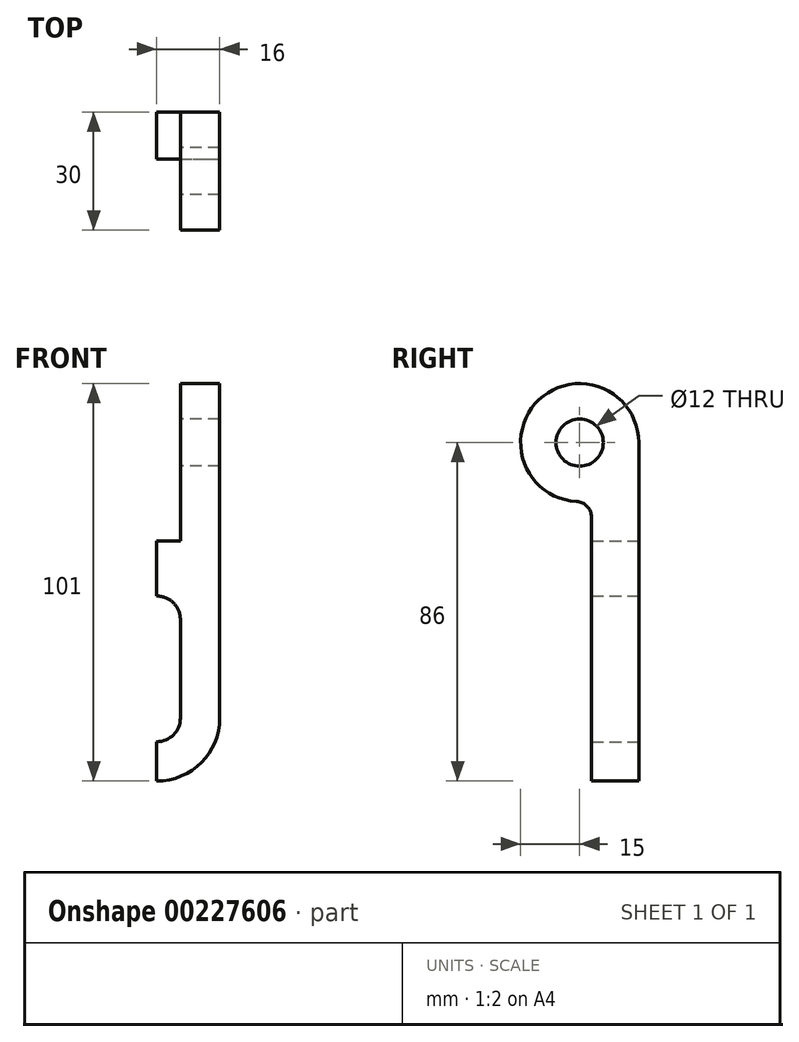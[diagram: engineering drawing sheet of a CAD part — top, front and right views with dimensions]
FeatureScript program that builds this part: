
annotation { "Feature Type Name" : "Feature", "Feature Type Description" : "" }
export const myFeature = defineFeature(function(context is Context, id is Id, definition is map)
    precondition{}
    {
        {
            var Q0;
            Q0=qCreatedBy(makeId("Front.planeOp"),FACE);
            var sketch = newSketch(context, id + "F0", { "sketchPlane" : qUnion([Q0])});
            skLineSegment(sketch, "E0", {"start": v(0, 0) * mm, "end": v(0, 0) * mm});
            skPoint(sketch, "E0.endSnap0", {"position": v(0, 0) * mm});
            skArc(sketch, "E1", {"start": v(-6, 0) * mm, "mid": v(0, -6) * mm, "end": v(6, 0) * mm});
            skArc(sketch, "E2", {"start": v(6, 25) * mm, "mid": v(0, 31) * mm, "end": v(-6, 25) * mm});
            skArc(sketch, "E3", {"start": v(-16, 0) * mm, "mid": v(0, -16) * mm, "end": v(16, 0) * mm});
            skLineSegment(sketch, "E4", {"start": v(-6, 25) * mm, "end": v(-6, 0) * mm});
            skLineSegment(sketch, "E5", {"start": v(6, 25) * mm, "end": v(6, 0) * mm});
            skLineSegment(sketch, "E6", {"start": v(-16, 85) * mm, "end": v(-6, 85) * mm});
            skLineSegment(sketch, "E7", {"start": v(-6, 85) * mm, "end": v(-6, 45) * mm});
            skLineSegment(sketch, "E8", {"start": v(-6, 45) * mm, "end": v(6, 45) * mm});
            skLineSegment(sketch, "E9", {"start": v(6, 45) * mm, "end": v(6, 85) * mm});
            skLineSegment(sketch, "E10", {"start": v(6, 85) * mm, "end": v(16, 85) * mm});
            skLineSegment(sketch, "E11", {"start": v(16, 0) * mm, "end": v(16, 85) * mm});
            skLineSegment(sketch, "E12", {"start": v(-16, 85) * mm, "end": v(-16, 0) * mm});
            skSolve(sketch);
        }
        {
            var Q0;
            Q0=makeQuery(id+"F0.imprint","IMPRINT",FACE,{"disambiguationData":[TD([[makeQuery(id+"F0.imprint","IMPRINT",EDGE,{"derivedFrom":sQuery(id+"F0.wireOp",EDGE,"E1")}),-1.0]])]});
            extrude(context, id + "F1", {"entities" : qUnion([Q0]), "depth" : 30 * mm});
        }
        {
            var Q0;
            Q0=qCreatedBy(makeId("Right.planeOp"),FACE);
            var sketch = newSketch(context, id + "F2", { "sketchPlane" : qUnion([Q0])});
            skLineSegment(sketch, "E13.0", {"start": v(-30, 0) * mm, "end": v(-30, 85) * mm, "construction": true});
            skLineSegment(sketch, "E14.0.0", {"start": v(0, 0) * mm, "end": v(0, 85) * mm, "construction": true});
            skLineSegment(sketch, "E14.0.1", {"start": v(0, 85) * mm, "end": v(-30, 85) * mm, "construction": true});
            skLineSegment(sketch, "E14.0.2", {"start": v(-30, 85) * mm, "end": v(-30, 0) * mm, "construction": true});
            skLineSegment(sketch, "E14.0.3", {"start": v(-30, 0) * mm, "end": v(0, 0) * mm, "construction": true});
            skLineSegment(sketch, "E15", {"start": v(0, -16) * mm, "end": v(-30, -16) * mm, "construction": true});
            skCircle(sketch, "E16", {"center": v(-15, 70) * mm, "radius": 6 * mm});
            skArc(sketch, "E17", {"start": v(0, 70) * mm, "mid": v(-25.32, 80.88) * mm, "end": v(-15.79, 55.02) * mm});
            skLineSegment(sketch, "E18", {"start": v(-12, 51.03) * mm, "end": v(-12, -16) * mm});
            skPoint(sketch, "E18.endSnap0", {"position": v(-15, -16) * mm});
            skLineSegment(sketch, "E19", {"start": v(-12, -16) * mm, "end": v(-30, -16) * mm});
            skLineSegment(sketch, "E20", {"start": v(-30, -16) * mm, "end": v(-30, 70) * mm});
            skPoint(sketch, "E21.visualSharp", {"position": v(-12, 55.3) * mm});
            skArc(sketch, "E21.filletArc", {"start": v(-12, 51.03) * mm, "mid": v(-13.1, 53.78) * mm, "end": v(-15.79, 55.02) * mm});
            skLineSegment(sketch, "E22", {"start": v(-12, -16) * mm, "end": v(0, -16) * mm});
            skLineSegment(sketch, "E23", {"start": v(0, 85) * mm, "end": v(-30, 85) * mm});
            skLineSegment(sketch, "E24", {"start": v(-30, 85) * mm, "end": v(-30, 70) * mm});
            skLineSegment(sketch, "E25", {"start": v(0, 85) * mm, "end": v(0, -16) * mm});
            skSolve(sketch);
        }
        {
            var Q0;
            Q0=makeQuery(id+"F2.imprint","IMPRINT",FACE,{"disambiguationData":[TD([[makeQuery(id+"F2.imprint","IMPRINT",EDGE,{"derivedFrom":sQuery(id+"F2.wireOp",EDGE,"E18")}),-1.0]])]});
            var Q1;
            {var subQ0=sQuery(id+"F2.wireOp",EDGE,"E24");Q1=makeQuery(id+"F2.imprint","IMPRINT",FACE,{"disambiguationData":[TD([[makeQuery(id+"F2.imprint","IMPRINT",EDGE,{"derivedFrom":subQ0}),1.0]])]});}
            var Q2;
            {var subQ0=sQuery(id+"F2.wireOp",EDGE,"E25");var subQ1=sQuery(id+"F2.wireOp",EDGE,"E17");var subQ2=makeQuery(id+"F2.imprint","INTERSECT",VERTEX,{"derivedFrom":[subQ1,subQ0]});Q2=makeQuery(id+"F2.imprint","IMPRINT",FACE,{"disambiguationData":[TD([[makeQuery(id+"F2.imprint","IMPRINT",EDGE,{"disambiguationData":[TD([[subQ2,-1.0]])],"derivedFrom":subQ1}),-1.0]])]});}
            extrude(context, id + "F3", {"entities" : qUnion([Q0, Q1, Q2]), "operationType" : NewBodyOperationType.REMOVE, "endBound" : BoundingType.SYMMETRIC, "oppositeDirection" : true, "depth" : 100 * mm});
        }
        {
            var Q0;
            Q0=makeQuery(id+"F2.imprint","IMPRINT",FACE,{"disambiguationData":[TD([[makeQuery(id+"F2.imprint","IMPRINT",EDGE,{"derivedFrom":sQuery(id+"F2.wireOp",EDGE,"E16")}),1.0]])]});
            extrude(context, id + "F4", {"entities" : qUnion([Q0]), "operationType" : NewBodyOperationType.REMOVE, "endBound" : BoundingType.SYMMETRIC, "depth" : 51 * mm});
        }
        {
            var Q0;
            Q0 = qSketchRegion(id + "F2", true);
            var Q1;
            Q1=makeQuery(id+"F1.opExtrude","SWEPT_FACE",FACE,{"disambiguationData":[OSD([sQuery(id+"F0.wireOp",EDGE,"E12")])]});
            extrude(context, id + "F5", {"entities" : qUnion([Q0, Q1]), "operationType" : NewBodyOperationType.REMOVE, "oppositeDirection" : true, "depth" : 25 * mm});
        }
    });
